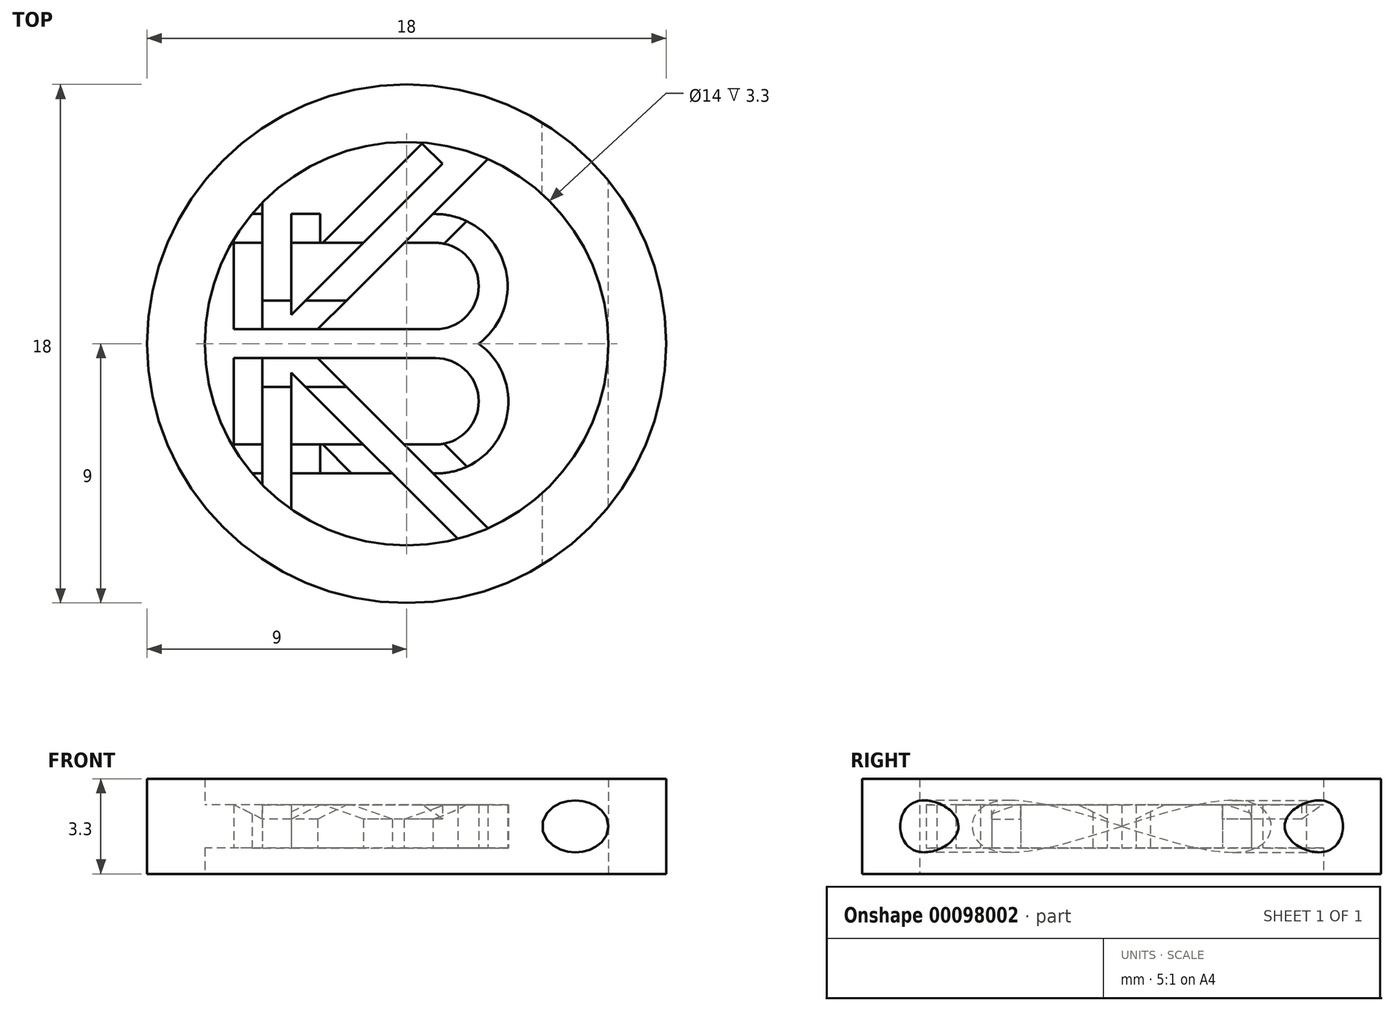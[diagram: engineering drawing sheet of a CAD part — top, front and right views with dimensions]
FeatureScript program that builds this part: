
annotation { "Feature Type Name" : "Feature", "Feature Type Description" : "" }
export const myFeature = defineFeature(function(context is Context, id is Id, definition is map)
    precondition{}
    {
        {
            var Q0;
            Q0=qCreatedBy(makeId("Top.planeOp"),FACE);
            var sketch = newSketch(context, id + "F0", { "sketchPlane" : qUnion([Q0])});
            skCircle(sketch, "E0", {"center": v(0, 0) * mm, "radius": 8 * mm});
            skLineSegment(sketch, "E1", {"start": v(-5, 6.24) * mm, "end": v(-5, -6.24) * mm, "construction": true});
            skLineSegment(sketch, "E2", {"start": v(-4, 6.93) * mm, "end": v(-4, -6.93) * mm, "construction": true});
            skLineSegment(sketch, "E3", {"start": v(-5, 0) * mm, "end": v(2.57, 7.57) * mm, "construction": true});
            skLineSegment(sketch, "E4", {"start": v(-5, 0) * mm, "end": v(2.57, -7.57) * mm, "construction": true});
            skLineSegment(sketch, "E5", {"start": v(-5, -1.41) * mm, "end": v(3.57, 7.16) * mm, "construction": true});
            skLineSegment(sketch, "E6", {"start": v(-5, 1.41) * mm, "end": v(3.57, -7.16) * mm, "construction": true});
            skLineSegment(sketch, "E7", {"start": v(-6.61, 4.5) * mm, "end": v(1, 4.5) * mm, "construction": true});
            skLineSegment(sketch, "E8", {"start": v(-7.2, 3.5) * mm, "end": v(1, 3.5) * mm, "construction": true});
            skLineSegment(sketch, "E9", {"start": v(-7.2, -3.5) * mm, "end": v(1, -3.5) * mm, "construction": true});
            skLineSegment(sketch, "E10", {"start": v(-6.61, -4.5) * mm, "end": v(1, -4.5) * mm, "construction": true});
            skLineSegment(sketch, "E11", {"start": v(-7.98, 0.5) * mm, "end": v(1, 0.5) * mm, "construction": true});
            skLineSegment(sketch, "E12", {"start": v(-7.98, -0.5) * mm, "end": v(1, -0.5) * mm, "construction": true});
            skArc(sketch, "E13", {"start": v(1, -3.5) * mm, "mid": v(2.5, -2) * mm, "end": v(1, -0.5) * mm, "construction": true});
            skArc(sketch, "E14", {"start": v(1, -4.5) * mm, "mid": v(3.5, -2) * mm, "end": v(1, 0.5) * mm, "construction": true});
            skArc(sketch, "E15", {"start": v(1, 0.5) * mm, "mid": v(2.5, 2) * mm, "end": v(1, 3.5) * mm, "construction": true});
            skArc(sketch, "E16", {"start": v(1, 4.5) * mm, "mid": v(3.5, 2) * mm, "end": v(1, -0.5) * mm, "construction": true});
            skLineSegment(sketch, "E17", {"start": v(-5, 3.5) * mm, "end": v(-5, 0.5) * mm});
            skLineSegment(sketch, "E18", {"start": v(-5, -0.5) * mm, "end": v(-5, -3.5) * mm});
            skLineSegment(sketch, "E19", {"start": v(-6.61, -4.5) * mm, "end": v(-5, -4.5) * mm});
            skLineSegment(sketch, "E20", {"start": v(-5, -4.5) * mm, "end": v(-5, -6.24) * mm});
            skLineSegment(sketch, "E21", {"start": v(-6.61, 4.5) * mm, "end": v(-5, 4.5) * mm});
            skLineSegment(sketch, "E22", {"start": v(-5, 4.5) * mm, "end": v(-5, 6.24) * mm});
            skLineSegment(sketch, "E23", {"start": v(-4, 6.93) * mm, "end": v(-4, 4.5) * mm});
            skLineSegment(sketch, "E24", {"start": v(-4, 4.5) * mm, "end": v(1, 4.5) * mm});
            skLineSegment(sketch, "E25", {"start": v(1, 3.5) * mm, "end": v(-0.09, 3.5) * mm});
            skLineSegment(sketch, "E26", {"start": v(-0.09, 3.5) * mm, "end": v(-3.09, 0.5) * mm});
            skLineSegment(sketch, "E27", {"start": v(-3.09, 0.5) * mm, "end": v(1, 0.5) * mm});
            skLineSegment(sketch, "E28", {"start": v(1, -0.5) * mm, "end": v(-3.09, -0.5) * mm});
            skLineSegment(sketch, "E29", {"start": v(-3.09, -0.5) * mm, "end": v(-0.09, -3.5) * mm});
            skLineSegment(sketch, "E30", {"start": v(-0.09, -3.5) * mm, "end": v(1, -3.5) * mm});
            skLineSegment(sketch, "E31", {"start": v(-1.5, 3.5) * mm, "end": v(-4, 3.5) * mm});
            skLineSegment(sketch, "E32", {"start": v(-4, 3.5) * mm, "end": v(-4, 1) * mm});
            skLineSegment(sketch, "E33", {"start": v(-4, 1) * mm, "end": v(-1.5, 3.5) * mm});
            skLineSegment(sketch, "E34", {"start": v(-4, -1) * mm, "end": v(-4, -3.5) * mm});
            skLineSegment(sketch, "E35", {"start": v(-4, -3.5) * mm, "end": v(-1.5, -3.5) * mm});
            skLineSegment(sketch, "E36", {"start": v(-1.5, -3.5) * mm, "end": v(-4, -1) * mm});
            skLineSegment(sketch, "E37", {"start": v(-4, -6.93) * mm, "end": v(-4, -4.5) * mm});
            skLineSegment(sketch, "E38", {"start": v(-4, -4.5) * mm, "end": v(-0.5, -4.5) * mm});
            skLineSegment(sketch, "E39", {"start": v(-0.5, -4.5) * mm, "end": v(2.57, -7.57) * mm});
            skLineSegment(sketch, "E40", {"start": v(2.57, 7.57) * mm, "end": v(-0.5, 4.5) * mm});
            skLineSegment(sketch, "E41", {"start": v(-0.5, 4.5) * mm, "end": v(-4, 4.5) * mm});
            skArc(sketch, "E42", {"start": v(2.5, 0) * mm, "mid": v(3.37, 2.8) * mm, "end": v(1, 4.5) * mm});
            skArc(sketch, "E43", {"start": v(1, -3.5) * mm, "mid": v(2.5, -2) * mm, "end": v(1, -0.5) * mm});
            skArc(sketch, "E44", {"start": v(1, 0.5) * mm, "mid": v(2.5, 2) * mm, "end": v(1, 3.5) * mm});
            skLineSegment(sketch, "E45", {"start": v(-7, 3.87) * mm, "end": v(-7, -3.87) * mm});
            skLineSegment(sketch, "E46", {"start": v(-5, 3.5) * mm, "end": v(-6, 3.5) * mm});
            skLineSegment(sketch, "E47", {"start": v(-6, 3.5) * mm, "end": v(-6, 0.5) * mm});
            skLineSegment(sketch, "E48", {"start": v(-6, 0.5) * mm, "end": v(-5, 0.5) * mm});
            skLineSegment(sketch, "E49", {"start": v(-5, -0.5) * mm, "end": v(-6, -0.5) * mm});
            skLineSegment(sketch, "E50", {"start": v(-6, -0.5) * mm, "end": v(-6, -3.5) * mm});
            skLineSegment(sketch, "E51", {"start": v(-6, -3.5) * mm, "end": v(-5, -3.5) * mm});
            skLineSegment(sketch, "E52", {"start": v(0.91, 4.5) * mm, "end": v(3.57, 7.16) * mm});
            skLineSegment(sketch, "E53", {"start": v(0.91, -4.5) * mm, "end": v(3.57, -7.16) * mm});
            skLineSegment(sketch, "E54", {"start": v(0.91, -4.5) * mm, "end": v(1, -4.5) * mm});
            skArc(sketch, "E55", {"start": v(1, -4.5) * mm, "mid": v(3.4, -2.8) * mm, "end": v(2.5, 0) * mm});
            skSolve(sketch);
        }
        {
            var Q0;
            Q0=qCreatedBy(makeId("Top.planeOp"),FACE);
            var sketch = newSketch(context, id + "F1", { "sketchPlane" : qUnion([Q0])});
            skCircle(sketch, "E56", {"center": v(0, 0) * mm, "radius": 9 * mm});
            skCircle(sketch, "E57", {"center": v(0, 0) * mm, "radius": 7 * mm});
            skSolve(sketch);
        }
        {
            var Q0;
            Q0=makeQuery(id+"F0.imprint","IMPRINT",FACE,{"disambiguationData":[TD([[makeQuery(id+"F0.imprint","IMPRINT",EDGE,{"derivedFrom":sQuery(id+"F0.wireOp",EDGE,"E17")}),1.0]])]});
            var Q1;
            {var subQ1=sQuery(id+"F0.wireOp",EDGE,"E24");Q1=makeQuery(id+"F0.imprint","IMPRINT",FACE,{"disambiguationData":[TD([[makeQuery(id+"F0.imprint","IMPRINT",EDGE,{"derivedFrom":subQ1}),1.0]])]});}
            extrude(context, id + "F2", {"entities" : qUnion([Q0, Q1]), "depth" : 1.5 * mm});
        }
        {
            var Q0;
            Q0=makeQuery(id+"F2.opExtrude","CAP_EDGE",EDGE,{"disambiguationData":[OSD([sQuery(id+"F0.wireOp",EDGE,"E29")])],"isStart":false});
            cPlane(context, id + "F3", {"entities" : qUnion([Q0]), "cplaneType" : CPlaneType.MID_PLANE, "offset" : 150 * mm, "width" : 150 * mm, "height" : 150 * mm});
        }
        {
            var Q0;
            Q0=makeQuery(id+"F2.opExtrude","CAP_EDGE",EDGE,{"disambiguationData":[OSD([sQuery(id+"F0.wireOp",EDGE,"E26")])],"isStart":false});
            cPlane(context, id + "F4", {"entities" : qUnion([Q0]), "cplaneType" : CPlaneType.MID_PLANE, "offset" : 150 * mm, "width" : 150 * mm, "height" : 150 * mm});
        }
        {
            var Q0;
            Q0=makeQuery(id+"F2.opExtrude","SWEPT_FACE",FACE,{"disambiguationData":[OSD([sQuery(id+"F0.wireOp",EDGE,"E31")])]});
            var sketch = newSketch(context, id + "F5", { "sketchPlane" : qUnion([Q0])});
            skLineSegment(sketch, "E58", {"start": v(-4, 1) * mm, "end": v(-3, 1.5) * mm});
            skSolve(sketch);
        }
        {
            var Q0;
            {var subQ0=sQuery(id+"F5.wireOp",EDGE,"E58");Q0=makeQuery(id+"F5.imprint","IMPRINT",FACE,{"disambiguationData":[TD([[makeQuery(id+"F5.imprint","IMPRINT",EDGE,{"derivedFrom":subQ0}),1.0]])]});}
            extrude(context, id + "F6", {"entities" : qUnion([Q0]), "operationType" : NewBodyOperationType.REMOVE, "oppositeDirection" : true, "depth" : 1 * mm});
        }
        {
            var Q0;
            Q0=makeQuery(id+"F2.opExtrude","SWEPT_FACE",FACE,{"disambiguationData":[OSD([sQuery(id+"F0.wireOp",EDGE,"E46")])]});
            var sketch = newSketch(context, id + "F7", { "sketchPlane" : qUnion([Q0])});
            skLineSegment(sketch, "E59", {"start": v(-5, 1) * mm, "end": v(-6, 1.5) * mm});
            skSolve(sketch);
        }
        {
            var Q0;
            {var subQ0=sQuery(id+"F7.wireOp",EDGE,"E59");Q0=makeQuery(id+"F7.imprint","IMPRINT",FACE,{"disambiguationData":[TD([[makeQuery(id+"F7.imprint","IMPRINT",EDGE,{"derivedFrom":subQ0}),-1.0]])]});}
            extrude(context, id + "F8", {"entities" : qUnion([Q0]), "operationType" : NewBodyOperationType.REMOVE, "oppositeDirection" : true, "depth" : 1 * mm});
        }
        {
            var Q0;
            Q0=makeQuery(id+"F2.opExtrude","SWEPT_FACE",FACE,{"disambiguationData":[OSD([sQuery(id+"F0.wireOp",EDGE,"E51")])]});
            var sketch = newSketch(context, id + "F9", { "sketchPlane" : qUnion([Q0])});
            skLineSegment(sketch, "E60", {"start": v(5, 1) * mm, "end": v(6, 1.5) * mm});
            skSolve(sketch);
        }
        {
            var Q0;
            {var subQ0=sQuery(id+"F9.wireOp",EDGE,"E60");Q0=makeQuery(id+"F9.imprint","IMPRINT",FACE,{"disambiguationData":[TD([[makeQuery(id+"F9.imprint","IMPRINT",EDGE,{"derivedFrom":subQ0}),1.0]])]});}
            extrude(context, id + "F10", {"entities" : qUnion([Q0]), "operationType" : NewBodyOperationType.REMOVE, "oppositeDirection" : true, "depth" : 1 * mm});
        }
        {
            var Q0;
            Q0=makeQuery(id+"F2.opExtrude","SWEPT_FACE",FACE,{"disambiguationData":[OSD([sQuery(id+"F0.wireOp",EDGE,"E35")])]});
            var sketch = newSketch(context, id + "F11", { "sketchPlane" : qUnion([Q0])});
            skLineSegment(sketch, "E61", {"start": v(4, 1) * mm, "end": v(3, 1.5) * mm});
            skSolve(sketch);
        }
        {
            var Q0;
            {var subQ0=sQuery(id+"F11.wireOp",EDGE,"E61");Q0=makeQuery(id+"F11.imprint","IMPRINT",FACE,{"disambiguationData":[TD([[makeQuery(id+"F11.imprint","IMPRINT",EDGE,{"derivedFrom":subQ0}),-1.0]])]});}
            extrude(context, id + "F12", {"entities" : qUnion([Q0]), "operationType" : NewBodyOperationType.REMOVE, "oppositeDirection" : true, "depth" : 1 * mm});
        }
        {
            var Q0;
            {var subQ0=sQuery(id+"F0.wireOp",EDGE,"E17");Q0=makeQuery(id+"F8.boolean.opBoolean","MERGE",FACE,{"derivedFrom":[makeQuery(id+"F2.opExtrude","SWEPT_FACE",FACE,{"disambiguationData":[OSD([subQ0])]}),makeQuery(id+"F2.opExtrude","SWEPT_FACE",FACE,{"disambiguationData":[OSD([sQuery(id+"F0.wireOp",EDGE,"E22")])]}),makeQuery(id+"F8.opExtrude","SWEPT_FACE",FACE,{"disambiguationData":[OSD([subQ0,sQuery(id+"F0.wireOp",EDGE,"E46")])]})]});}
            var sketch = newSketch(context, id + "F13", { "sketchPlane" : qUnion([Q0])});
            skLineSegment(sketch, "E62", {"start": v(-1.5, 1.5) * mm, "end": v(-0.5, 1) * mm});
            skSolve(sketch);
        }
        {
            var Q0;
            {var subQ0=sQuery(id+"F13.wireOp",EDGE,"E62");Q0=makeQuery(id+"F13.imprint","IMPRINT",FACE,{"disambiguationData":[TD([[makeQuery(id+"F13.imprint","IMPRINT",EDGE,{"derivedFrom":subQ0}),1.0]])]});}
            extrude(context, id + "F14", {"entities" : qUnion([Q0]), "operationType" : NewBodyOperationType.REMOVE, "oppositeDirection" : true, "depth" : 3 * mm});
        }
        {
            var Q0;
            {var subQ0=sQuery(id+"F0.wireOp",EDGE,"E18");Q0=makeQuery(id+"F10.boolean.opBoolean","MERGE",FACE,{"derivedFrom":[makeQuery(id+"F2.opExtrude","SWEPT_FACE",FACE,{"disambiguationData":[OSD([subQ0])]}),makeQuery(id+"F2.opExtrude","SWEPT_FACE",FACE,{"disambiguationData":[OSD([sQuery(id+"F0.wireOp",EDGE,"E20")])]}),makeQuery(id+"F10.opExtrude","SWEPT_FACE",FACE,{"disambiguationData":[OSD([subQ0,sQuery(id+"F0.wireOp",EDGE,"E51")])]})]});}
            var sketch = newSketch(context, id + "F15", { "sketchPlane" : qUnion([Q0])});
            skLineSegment(sketch, "E63", {"start": v(0.5, 1) * mm, "end": v(1.5, 1.5) * mm});
            skSolve(sketch);
        }
        {
            var Q0;
            {var subQ0=sQuery(id+"F15.wireOp",EDGE,"E63");Q0=makeQuery(id+"F15.imprint","IMPRINT",FACE,{"disambiguationData":[TD([[makeQuery(id+"F15.imprint","IMPRINT",EDGE,{"derivedFrom":subQ0}),1.0]])]});}
            extrude(context, id + "F16", {"entities" : qUnion([Q0]), "operationType" : NewBodyOperationType.REMOVE, "oppositeDirection" : true, "depth" : 3 * mm});
        }
        {
            var Q0;
            Q0=qCreatedBy(id+"F4.planeOp",FACE);
            var sketch = newSketch(context, id + "F17", { "sketchPlane" : qUnion([Q0])});
            skLineSegment(sketch, "E64", {"start": v(-4.54, 1.5) * mm, "end": v(-3.54, 1.5) * mm});
            skLineSegment(sketch, "E65", {"start": v(-3.54, 1.5) * mm, "end": v(-3.54, 1) * mm});
            skLineSegment(sketch, "E66", {"start": v(-3.54, 1) * mm, "end": v(-4.54, 1.5) * mm});
            skLineSegment(sketch, "E67", {"start": v(-1.54, 1.5) * mm, "end": v(-2.54, 1.5) * mm});
            skLineSegment(sketch, "E68", {"start": v(-2.54, 1.5) * mm, "end": v(-2.54, 1) * mm});
            skLineSegment(sketch, "E69", {"start": v(-2.54, 1) * mm, "end": v(-1.54, 1.5) * mm});
            skSolve(sketch);
        }
        {
            var Q0;
            Q0=makeQuery(id+"F17.imprint","IMPRINT",FACE,{"disambiguationData":[TD([[makeQuery(id+"F17.imprint","IMPRINT",EDGE,{"derivedFrom":sQuery(id+"F17.wireOp",EDGE,"E64")}),-1.0]])]});
            var Q1;
            Q1=makeQuery(id+"F17.imprint","IMPRINT",FACE,{"disambiguationData":[TD([[makeQuery(id+"F17.imprint","IMPRINT",EDGE,{"derivedFrom":sQuery(id+"F17.wireOp",EDGE,"E67")}),1.0]])]});
            extrude(context, id + "F18", {"entities" : qUnion([Q0, Q1]), "operationType" : NewBodyOperationType.REMOVE, "oppositeDirection" : true, "depth" : 5 * mm});
        }
        {
            var Q0;
            Q0=qCreatedBy(id+"F3.planeOp",FACE);
            var sketch = newSketch(context, id + "F19", { "sketchPlane" : qUnion([Q0])});
            skLineSegment(sketch, "E70", {"start": v(-1.54, 1.5) * mm, "end": v(-2.54, 1.5) * mm});
            skLineSegment(sketch, "E71", {"start": v(-2.54, 1.5) * mm, "end": v(-2.54, 1) * mm});
            skLineSegment(sketch, "E72", {"start": v(-2.54, 1) * mm, "end": v(-1.54, 1.5) * mm});
            skLineSegment(sketch, "E73", {"start": v(-4.54, 1.5) * mm, "end": v(-3.54, 1.5) * mm});
            skLineSegment(sketch, "E74", {"start": v(-3.54, 1.5) * mm, "end": v(-3.54, 1) * mm});
            skLineSegment(sketch, "E75", {"start": v(-3.54, 1) * mm, "end": v(-4.54, 1.5) * mm});
            skSolve(sketch);
        }
        {
            var Q0;
            Q0=makeQuery(id+"F19.imprint","IMPRINT",FACE,{"disambiguationData":[TD([[makeQuery(id+"F19.imprint","IMPRINT",EDGE,{"derivedFrom":sQuery(id+"F19.wireOp",EDGE,"E70")}),1.0]])]});
            var Q1;
            Q1=makeQuery(id+"F19.imprint","IMPRINT",FACE,{"disambiguationData":[TD([[makeQuery(id+"F19.imprint","IMPRINT",EDGE,{"derivedFrom":sQuery(id+"F19.wireOp",EDGE,"E73")}),-1.0]])]});
            extrude(context, id + "F20", {"entities" : qUnion([Q0, Q1]), "operationType" : NewBodyOperationType.REMOVE, "depth" : 5 * mm});
        }
        {
            var Q0;
            Q0=qSketchRegion(id+"F1",true);
            extrude(context, id + "F21", {"entities" : qUnion([Q0]), "operationType" : NewBodyOperationType.ADD, "depth" : 2.4 * mm, "hasSecondDirection" : true, "secondDirectionOppositeDirection" : true, "secondDirectionDepth" : .9 * mm});
        }
        {
            var Q0;
            Q0=qCreatedBy(makeId("Front.planeOp"),FACE);
            var sketch = newSketch(context, id + "F22", { "sketchPlane" : qUnion([Q0])});
            skEllipse(sketch, "E76", {"center": v(5.85, 0.75) * mm, "majorRadius": 1.15 * mm, "minorRadius": 0.9 * mm, "majorAxis": v(1, 0)});
            skSolve(sketch);
        }
        {
            var Q0;
            Q0=makeQuery(id+"F22.imprint","IMPRINT",FACE,{"disambiguationData":[TD([[makeQuery(id+"F22.imprint","IMPRINT",EDGE,{"derivedFrom":sQuery(id+"F22.wireOp",EDGE,"E76")}),1.0]])]});
            extrude(context, id + "F23", {"entities" : qUnion([Q0]), "operationType" : NewBodyOperationType.REMOVE, "depth" : 25 * mm, "hasSecondDirection" : true, "secondDirectionOppositeDirection" : true, "secondDirectionDepth" : 25 * mm});
        }
    });
